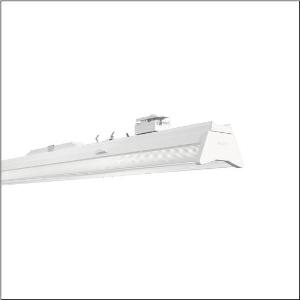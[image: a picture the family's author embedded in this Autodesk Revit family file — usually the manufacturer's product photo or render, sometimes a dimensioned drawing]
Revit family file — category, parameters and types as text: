
# Revit family: licross_r__21_performance_mo_51td16vn375g_e9bb
name_source: partatom
category: Lighting Fixtures
units: mm (PartAtom-declared; Revit-internal decimal feet)

## family parameters
Cut with Voids When Loaded = No
Host = Face
Light Source = No
Part Type = Normal
Room Calculation Point = No
Round Connector Dimension = Use Diameter
Shared = No

## types (1)
- --- (1 x LED, 7700 lm, 44.1 W, 3000K)
    Apparent Load = 44 VA
    CIE Flux Codes = 66 88 96 79 100
    Color Rendering = 80
    Color Temperature = 3000K
    Default Elevation = 1800 mm
    Description = Licross® 21 Performance MO, luminaire insert, of sheet steel, galvanised, coil coated, white, length: 1.500mm, width: 120mm, height: 123mm, LED rated luminous flux: 7.700lm, light colour: 830, SDCM (Standard Deviation of Colour Matching)MacAdam ≤ 2 SDCM (initial), control gear: DALI 2, CLO, with plug, 5-pole, with phase selection, mains connection: 220..240V, AC, 50/60Hz, start of lifetime: 44W, end of service life: 49W, internal wiring halogen-free, primary light control with lens, of plastic, primary optical cover: cover, of PMMA, light emission: direct/indirect distribution, primary light characteristic: symmetric, protection rating (complete): IP54, insulation class (complete): insulation class I (protective earthing), certification: CE, ENEC, VDE, UKCA, protection symbol: D if used in an environment with non-conductive dust loads with corresponding accessories, impact resistance: IK06, permissible ambient temperature for indoor applications: -25..+35°C, corresponds to IFS (International Featured Standards) requirements for safety and quality in the food industry, reducing of maximum allowable ambient temperature of 5°C with ceiling mounting, LABS conformity tested according to VDMA 24364:2018-05, packaging unit: 1 piece
    Height = 114 mm
    Lamp = 1 x LED
    Lamp Light Flux = 7700 lm
    Lamp Power = 44.1 W
    Lamp count = 1
    Length = 1500 mm
    Luminous efficacy = 175 lm/W
    Manufacturer = Siteco
    ModVariant = No
    Model = 51TD16VN375G
    Mounting Place = Ceiling
    Mounting Type = Pendant
    Number of Poles = 1
    OnlyDefault = Yes
    Power Factor = 1
    Product Name = Licross® 21 Performance MO
    Product group = luminaire insert | ceiling pendant
    ProductGroupID = 901
    Protection Class = Protection class I
    Protection Degree = IP 54
    RLX_Detail_Level = 1
    RLX_Emergency_Light_Flux = 0 lm
    RLX_Emergency_Type = 0
    RLX_Emergency_Type_DB = No
    RlxData = <blob elided: 34109 chars, md5=b81961a5>
    Socket = socket
    Standby Power = 0 W
    System Light Flux = 7700 lm
    System Power = 44 W
    Type Comments = factory setting: luminous flux: 100 % | dim-lin: 254 | 294 mA
    Type Image = l_1256138.jpg
    URL = http://relux.com
    VarID = @adj_004423
    Voltage = 0 V
    Weight = 0.00 kg
    Width = 120 mm

## geometry (parser evidence)
native form markers: Blend x4, Sweep x12
no freeform markers — native parametric forms only
